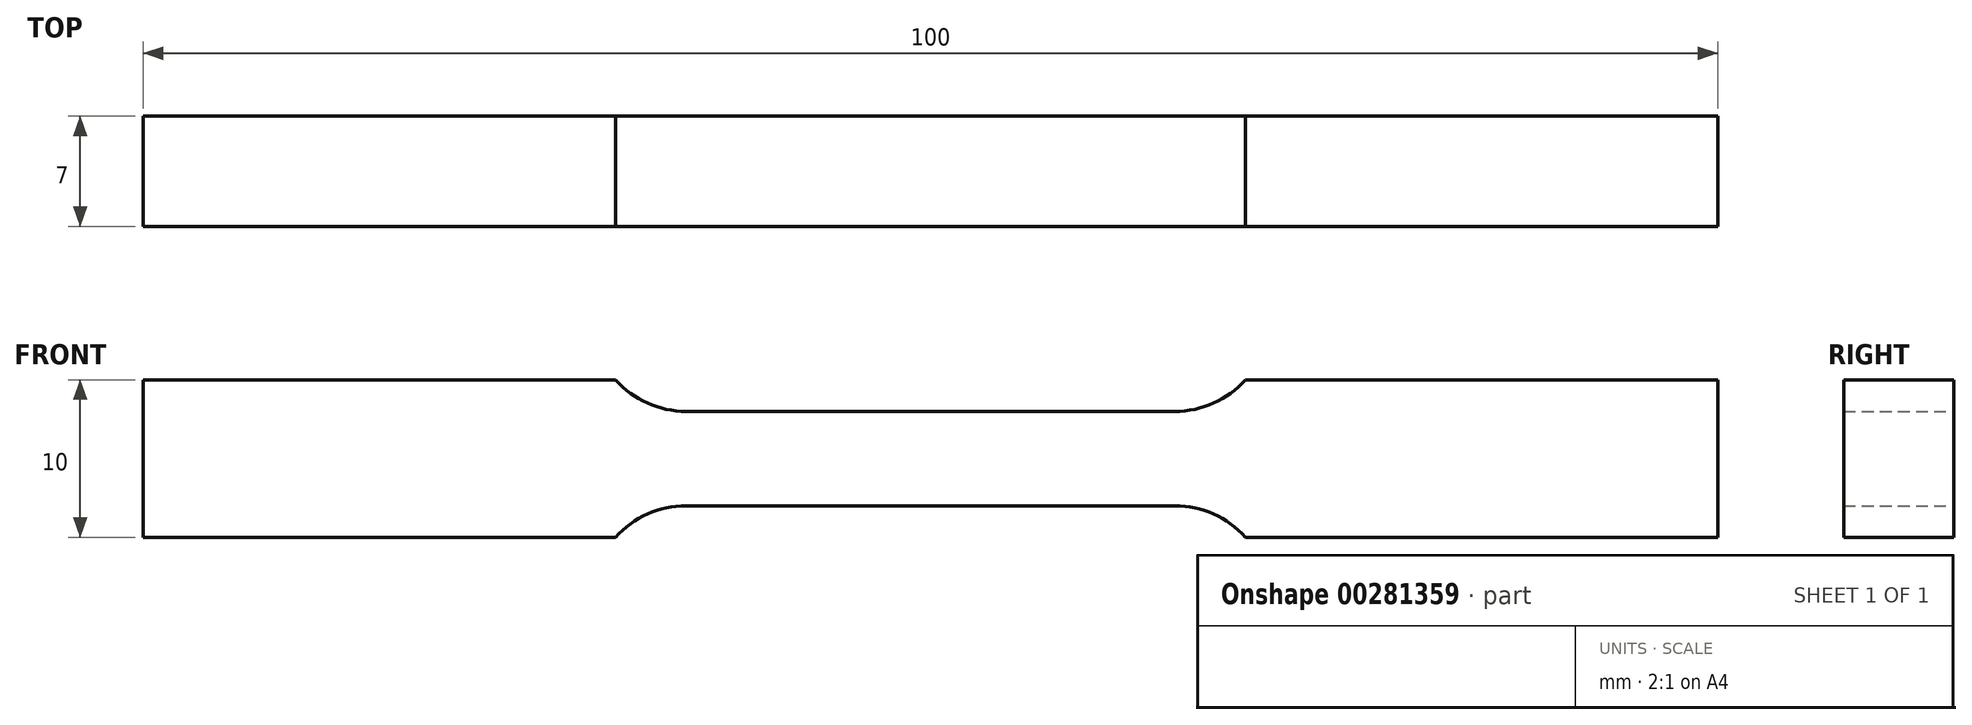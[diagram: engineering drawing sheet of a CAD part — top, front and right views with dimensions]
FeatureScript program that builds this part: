
annotation { "Feature Type Name" : "Feature", "Feature Type Description" : "" }
export const myFeature = defineFeature(function(context is Context, id is Id, definition is map)
    precondition{}
    {
        {
            var Q0;
            Q0=qCreatedBy(makeId("Front.planeOp"),FACE);
            var sketch = newSketch(context, id + "F0", { "sketchPlane" : qUnion([Q0])});
            skLineSegment(sketch, "E0", {"start": v(0, 3) * mm, "end": v(15.53, 3) * mm});
            skArc(sketch, "E1", {"start": v(15.53, 3) * mm, "mid": v(17.98, 3.52) * mm, "end": v(20, 5) * mm});
            skLineSegment(sketch, "E2", {"start": v(20, 5) * mm, "end": v(50, 5) * mm});
            skLineSegment(sketch, "E3", {"start": v(50, 5) * mm, "end": v(50, 0) * mm});
            skLineSegment(sketch, "E4.MirrorCS", {"start": v(0, -3) * mm, "end": v(15.53, -3) * mm});
            skLineSegment(sketch, "E5.MirrorCS", {"start": v(50, -5) * mm, "end": v(50, 0) * mm});
            skLineSegment(sketch, "E6.MirrorCS", {"start": v(20, -5) * mm, "end": v(50, -5) * mm});
            skArc(sketch, "E7.MirrorCS", {"start": v(15.53, -3) * mm, "mid": v(17.98, -3.52) * mm, "end": v(20, -5) * mm});
            skArc(sketch, "E8.MirrorCS", {"start": v(-15.53, -3) * mm, "mid": v(-17.98, -3.52) * mm, "end": v(-20, -5) * mm});
            skLineSegment(sketch, "E9.MirrorCS", {"start": v(-20, -5) * mm, "end": v(-50, -5) * mm});
            skArc(sketch, "E10.MirrorCS", {"start": v(-15.53, 3) * mm, "mid": v(-17.98, 3.52) * mm, "end": v(-20, 5) * mm});
            skLineSegment(sketch, "E11.MirrorCS", {"start": v(-20, 5) * mm, "end": v(-50, 5) * mm});
            skLineSegment(sketch, "E12.MirrorCS", {"start": v(-50, -5) * mm, "end": v(-50, 0) * mm});
            skLineSegment(sketch, "E13.MirrorCS", {"start": v(0, -3) * mm, "end": v(-15.53, -3) * mm});
            skLineSegment(sketch, "E14.MirrorCS", {"start": v(-50, 5) * mm, "end": v(-50, 0) * mm});
            skLineSegment(sketch, "E15.MirrorCS", {"start": v(0, 3) * mm, "end": v(-15.53, 3) * mm});
            skSolve(sketch);
        }
        {
            var Q0;
            Q0 = qSketchRegion(id + "F0", true);
            extrude(context, id + "F1", {"entities" : qUnion([Q0]), "depth" : 7 * mm});
        }
    });
